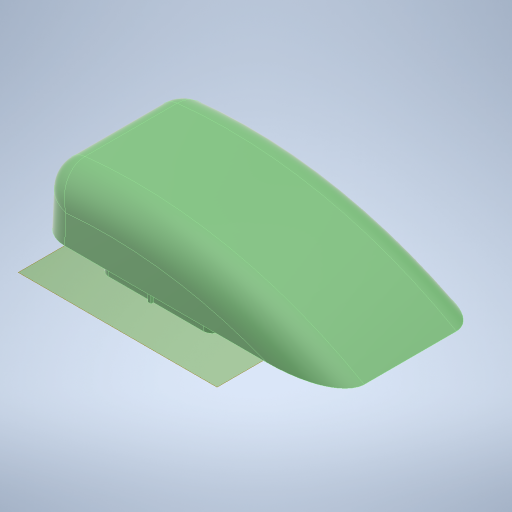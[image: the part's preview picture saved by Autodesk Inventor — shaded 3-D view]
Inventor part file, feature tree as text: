
AUTODESK INVENTOR PART (.ipt)
format: ipt  version: 2023 (Build 270158000, 158)  size: 436,736 bytes
history: native  units: in
note: dims shown in document units (in); Inventor stores cm internally (conversion verified against a paired STEP export)
features: extrude x2, fillet x2, shell x2, plane x2, sketch x2
ambient origin geometry x8: Origin, YZ Plane, XZ Plane, XY Plane, X Axis, Y Axis, Z Axis, Center Point
bodies: Body1 (feature_tree)
feature tree (10):
  extrude  "Extrusion1"  Depth=0.5in
  fillet  "Fillet1"  Radius=0.07in
  shell  "Shell1"  Thickness=0.65in
  plane  "Work Plane1"
  sketch  "Sketch5"  dims[d14=1.9in d15=1.5in d22=0.99in d23=0.05in d24=0.04in d26=0.99in d27=0.05in d28=0.05in d29=0.05in d32=0.28in d38=1.5in d39=0.0in d40=0.04in d41=0.05in d42=90.0deg d43=0.28in d44=0.04in d45=0.05in d46=0.28in d47=0.04in d48=0.05in d49=0.28in d50=0.05in d51=0.15in d18=0.5in d19=0.0344in d20=0.5in d21=0.0344in]
  plane  "Work Plane2"
  extrude  "Extrusion4"  Depth=0.15in
  shell  "Shell3"  Thickness=0.99in
  fillet  "Fillet3"  Radius=0.05in
  sketch  "Sketch2"  dims[d6=5.04in d7=0.03in d8=0.64in d9=2.55in d10=0.0in d11=0.5in d12=0.07in d13=0.65in]
